# Revit family: Camera-Security-Panasonic-Super_Dynamic-Vandal_Resistant-Waterproof-Dome-AI-Network-S2536LSeriesX
name_source: partatom
category: Security Devices
units: mm (PartAtom-declared; Revit-internal decimal feet)

## family parameters
Cut with Voids When Loaded = No
Host = Face
Maintain Annotation Orientation = No
OmniClass Number = 23.85.10.14.11
OmniClass Title = Cameras
Part Type = Normal
Room Calculation Point = No
Round Connector Dimension = Use Diameter
Shared = No

## types (2) — shared parameters
Alarm Input Or Output Specification = ALARM IN 1 (Alarm input 1/ Black & white input/ Auto time adjustment input) (x1), ALARM IN 2 (Alarm input 2/ ALARM OUT) (x1), ALARM IN 3 (Alarm input 3/ AUX OUT) (x1)
Angle Of View = 113
Audio In = ø3.5 mm stereo mini jack
Audio Out = ø3.5 mm stereo mini jack (monaural output)
Communication Ports = 10Base-T / 100Base-TX, RJ45 connector
Date Last Modified = 2021/09/02
Day Or Night = Yes
Diameter = 6.063 "
Equipment Abbreviation = SC
Family Version = 1.0.0
HFOV Max 169 = 113.00°
HFOV Max 43 = 82.00°
HFOV Min 169 = 36.00°
HFOV Min 43 = 26.00°
Has POE = Yes
Height = 4.134 "
IP Or Analog = IP
Indoor Or Outdoor = Outdoor
Manufacturer = Panasonic
Minimum Illumination = 0.007 lx
Model Disclaimer = Contact Panasonic for more information
Mounting Positions = Mount Dependent or Surface Mount
Operational Humidity = 10 to 100 % (no condensation)
Operational Temperature = -40 °C to +60 °C (-40 °F to 140 °F) (Power On range : –30 °C to +60 °C {–22 °F to +140 °F})
Pan Max = 166.00°
Pan Min = -194.00°
Panning Range = -194 to +166°
Product Documentation Link = https://bizpartner.panasonic.net
Product Material = Paint - Panasonic -i-Pro White
Product Page URL = https://security.panasonic.com
Provide Feedback = https://www.surveymonkey.com
Regulatory Compliance = UL (UL62368-1), c-UL (CSA C22.2 No.62368-1), CE, IEC62368-1, FCC (Part15 ClassA), ICES-003 ClassA, EN55032 ClassB, EN55035
Shock Resistance = 50J (IEC 60068-2-75 compliant), IK10 (IEC 62262)
Storage Temperature = -40 °C to +60 °C (-40 °F to 140 °F)
Super Dynamic Range = Yes
Tilt Max = 85.00°
Tilt Min = -30.00°
Tilting Range = -30 to +85°
URL = http://security.panasonic.com
VFOV Max 169 = 60.00°
VFOV Max 43 = 60.00°
VFOV Min 169 = 20.00°
VFOV Min 43 = 20.00°
Vandal Resistant = Yes
Water and Dust Resistance = IP66, IEC60529 measuring standard compatible, Type 4X(UL50), NEMA 4X compliant
Wide Dynamic Range = Yes
Yaw Max = 100.00°
Yaw Min = -100.00°
Yawing Range = ±100°
z Base Radius = 3.031 "
z Const Pan Handle Length = 19.488 "
z Const Tilt Base Length = 9.843 "
z Const Tilt Base2 Length = 19.685 "
z Const Tilt Handle Length = 11.811 "
z Const Yaw Base Length = 10.236 "
z Const Yaw Base2 Length = 17.323 "
z Const Yaw Handle Length = 9.252 "
z Dome Radius = 1.654 "
z VV Viewpoint Depth Max = 1.283 "
z VV Viewpoint Depth Min = 1.283 "
zero-valued in all types: Default Elevation

## per-type parameters (varying)
| type | Description | Part Description |
| WV-S2536L | Security Camera, Fixed Dome, AI, Network, Super Dynamic Vandal Resistant  Weatherproof, FullHD WV-S2536L | Security Camera, Fixed Dome, AI, Network, Super Dynamic Vandal Resistant  Weatherproof, FullHD WV-S2536L |
| WV-S2536LN | Security Camera, Fixed Dome, AI, Network, Super Dynamic Vandal Resistant  Weatherproof, FullHD WV-S2536LN | Security Camera, Fixed Dome, AI, Network, Super Dynamic Vandal Resistant  Weatherproof, FullHD WV-S2536LN |

note: column(s) folded — value = type name in every type: Model, Part Number

## geometry (parser evidence)
native form markers: Blend x2, Sweep x7
no freeform markers — native parametric forms only
